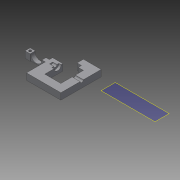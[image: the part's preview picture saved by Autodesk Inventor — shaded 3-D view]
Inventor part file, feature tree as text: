
AUTODESK INVENTOR PART (.ipt)
format: ipt  version: 2016 (Build 200138000, 138)  size: 208,384 bytes
history: native  units: mm
features: sketch x10, other x3, plane x1
ambient origin geometry x8: Origin, YZ Plane, XZ Plane, XY Plane, X Axis, Y Axis, Z Axis, Center Point
bodies: Solid1 (feature_tree)
feature tree (14):
  other  "gear frame 1.ipt"
  other  "Solid1::gear frame 1.ipt"
  other  "TaggingFeature1"
  sketch  "Sketch1"  dims[d0=10.0mm]
  sketch  "Sketch2"  dims[d1=2.0mm d2=1.0mm d3=20.0mm d4=16.0mm d5=10.0mm d6=40.0mm d7=25.0mm d8=50.0mm d9=20.0mm d10=20.0mm d11=15.0mm d12=14.0mm d13=25.0mm d14=20.0mm d15=0.0mm d16=34.925mm d18=0.0mm d19=16.0mm d20=16.0mm d22=0.0mm d23=8.0mm d25=0.0mm d26=10.0mm d27=95.0mm d28=0.0mm d29=22.0mm d30=7.0mm d31=0.0mm d32=22.0mm d33=15.0mm d34=0.0mm d35=16.0mm d36=16.0mm d38=0.0mm d39=8.0mm d41=0.0mm d42=8.0mm d43=8.0mm d46=8.0mm d47=25.0mm d48=8.0mm d49=8.0mm d50=12.0mm d51=15.0mm d52=15.0mm d53=8.0mm d54=40.0mm d55=10.0mm d57=0.0mm d58=5.0mm d61=10.0mm d64=5.0mm d67=5.0mm d70=10.0mm d73=10.0mm d76=10.0mm d79=5.0mm]
  sketch  "Sketch3"
  sketch  "Sketch4"
  sketch  "Sketch5"
  sketch  "Sketch6"
  sketch  "Sketch7"
  sketch  "Sketch8"
  sketch  "Sketch9"
  sketch  "Sketch10"
  plane  "Work Plane1"
